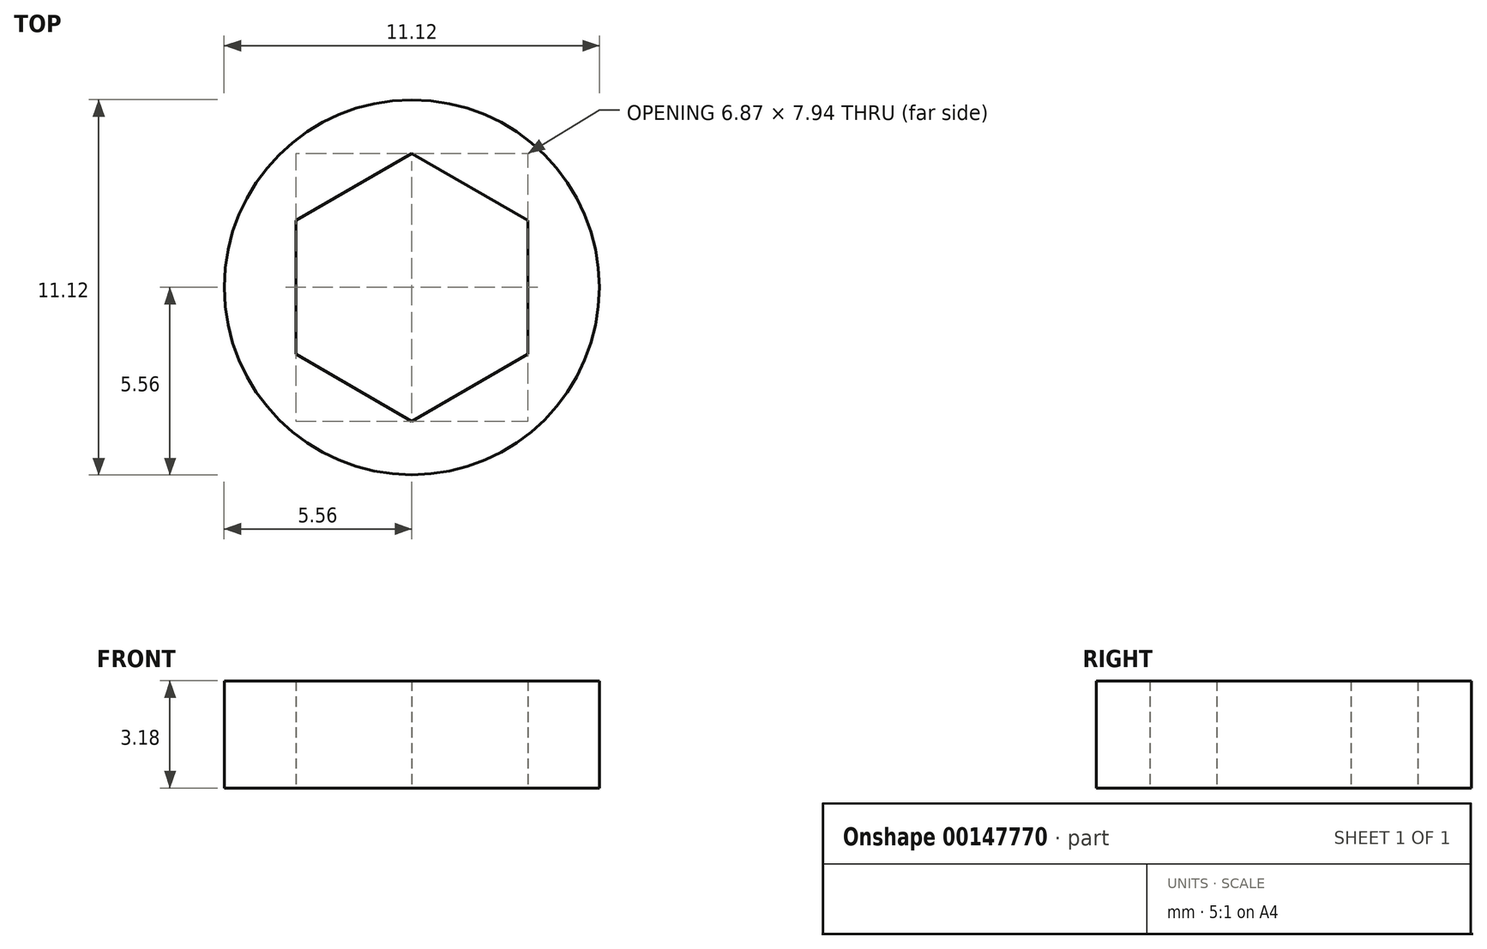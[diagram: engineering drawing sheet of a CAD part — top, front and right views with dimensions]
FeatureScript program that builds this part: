
annotation { "Feature Type Name" : "Feature", "Feature Type Description" : "" }
export const myFeature = defineFeature(function(context is Context, id is Id, definition is map)
    precondition{}
    {
        {
            var Q0;
            Q0=qCreatedBy(makeId("Top.planeOp"),FACE);
            var sketch = newSketch(context, id + "F0", { "sketchPlane" : qUnion([Q0])});
            skCircle(sketch, "E0.cCircle", {"center": v(0, 0) * mm, "radius": 3.97 * mm, "construction": true});
            skLineSegment(sketch, "E0.0", {"start": v(0, -3.97) * mm, "end": v(-3.44, -1.98) * mm});
            skLineSegment(sketch, "E0.1", {"start": v(-3.44, -1.98) * mm, "end": v(-3.44, 1.98) * mm});
            skLineSegment(sketch, "E0.2", {"start": v(-3.44, 1.98) * mm, "end": v(0, 3.97) * mm});
            skLineSegment(sketch, "E0.3", {"start": v(0, 3.97) * mm, "end": v(3.44, 1.98) * mm});
            skLineSegment(sketch, "E0.4", {"start": v(3.44, 1.98) * mm, "end": v(3.44, -1.98) * mm});
            skLineSegment(sketch, "E0.5", {"start": v(3.44, -1.98) * mm, "end": v(0, -3.97) * mm});
            skCircle(sketch, "E1", {"center": v(0, 0) * mm, "radius": 5.56 * mm});
            skSolve(sketch);
        }
        {
            var Q0;
            Q0=qSketchRegion(id+"F0",true);
            extrude(context, id + "F1", {"entities" : qUnion([Q0]), "depth" : 3.17 * mm});
        }
    });
